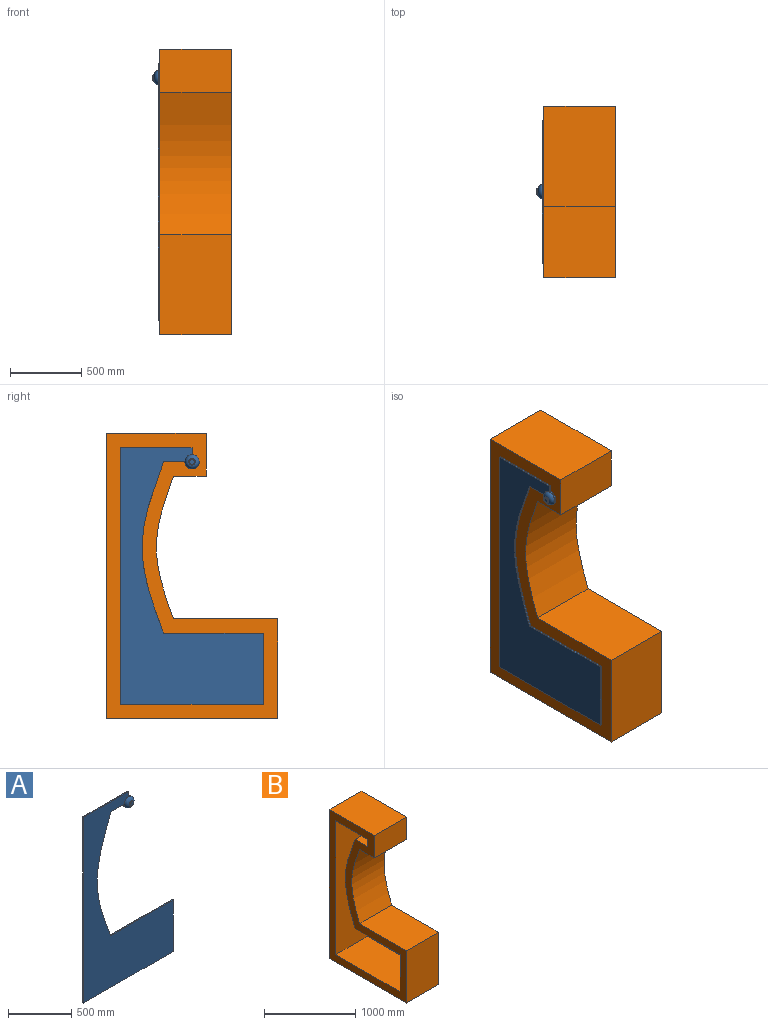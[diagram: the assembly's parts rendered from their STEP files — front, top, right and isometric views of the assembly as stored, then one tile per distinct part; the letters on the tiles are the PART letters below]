
ASSEMBLY  parts=2 mates=1
PART A: 15 faces, bbox 1000x50x1800 mm
  f0: plane 1000x10mm, normal (0,0,-1), area 10000mm2, adj f1,f7,f8,f9
  f1: plane 1800x10mm, normal (-1,0,0), area 18000mm2, adj f0,f2,f8,f9
  f2: plane 500x10mm, normal (0,0,1), area 5000mm2, adj f1,f3,f8,f9
  f3: plane 50x10mm, normal (1,0,0), area 500mm2, adj f2,f8,f9,f11
  f4: plane 150x10mm, normal (0,0,-1), area 1500mm2, adj f5,f8,f9,f11
  f5: extruded ~1200x150mm, area 12438.6mm2, adj f4,f6,f8,f9
  f6: plane 700x10mm, normal (0,0,1), area 7000mm2, adj f5,f7,f8,f9
  f7: plane 500x10mm, normal (1,0,0), area 5000mm2, adj f0,f6,f8,f9
  f8: plane 1800x1000mm, normal (0,1,0), area 803391.4mm2, adj f0,f1,f2,f3,f4,f5,f6,f7
  f9: plane 1800x1000mm, normal (0,-1,0), area 795537.4mm2, adj f0,f1,f2,f3,f4,f5,f6,f7
  f10: torus R=20mm, axis (0,-1,0), area 11576.6mm2, adj f9,f11,f12
  f11: cylinder r=50mm len=100mm, axis (0,-1,0), area 2356.2mm2, adj f3,f4,f8,f10
  f12: cone r=20mm half-angle=45deg, axis (0,-1,0), area 269.8mm2, adj f10,f14
  f13: plane 35.86x35.86mm, normal (0,-1,0), area 1009.9mm2, adj f14
  f14: torus R=17.93mm, axis (0,-1,0), area 1595.3mm2, adj f12,f13
PART B: 19 faces, bbox 500x1200x2000 mm
  f0: plane 495x200mm, normal (0,0,1), area 99000mm2, adj f1,f12,f17,f18
  f1: extruded ~1200x495mm, area 615712.1mm2, adj f0,f2,f12,f18
  f2: plane 700x495mm, normal (0,0,-1), area 346500mm2, adj f1,f12,f13,f18
  f3: plane 730.6x500mm, normal (0,0,1), area 365302.1mm2, adj f4,f8,f11,f12
  f4: plane 700x500mm, normal (0,-1,0), area 350000mm2, adj f3,f5,f11,f12
  f5: plane 1200x500mm, normal (0,0,-1), area 600000mm2, adj f4,f6,f11,f12
  f6: plane 2000x500mm, normal (0,1,0), area 1000000mm2, adj f5,f7,f11,f12
  f7: plane 700x500mm, normal (0,0,1), area 350000mm2, adj f6,f9,f11,f12
  f8: extruded ~1000x500mm, area 516859.4mm2, adj f3,f10,f11,f12
  f9: plane 500x300mm, normal (0,-1,0), area 150000mm2, adj f7,f10,f11,f12
  f10: plane 500x230.6mm, normal (0,0,-1), area 115302.1mm2, adj f8,f9,f11,f12
  f11: plane 2000x1200mm, normal (1,0,0), area 1444454mm2, adj f3,f4,f5,f6,f7,f8,f9,f10
  f12: plane 2000x1200mm, normal (-1,0,0), area 646953.1mm2, adj f0,f1,f2,f3,f4,f5,f6,f7
  f13: plane 500x495mm, normal (0,1,0), area 247500mm2, adj f2,f12,f14,f18
  f14: plane 1000x495mm, normal (0,0,1), area 495000mm2, adj f12,f13,f15,f18
  f15: plane 1800x495mm, normal (0,-1,0), area 891000mm2, adj f12,f14,f16,f18
  f16: plane 500x495mm, normal (0,0,-1), area 247500mm2, adj f12,f15,f17,f18
  f17: plane 495x100mm, normal (0,1,0), area 49500mm2, adj f0,f12,f16,f18
  f18: plane 1800x1000mm, normal (-1,0,0), area 797500.9mm2, adj f0,f1,f2,f13,f14,f15,f16,f17
PLACE A rot(axis=(0,0,-1),90deg) t=(-1138.81,-1209.02,571.63)mm
PLACE B t=(-648.81,-1085.99,49.41)mm
MATE fastened A.f8 <-> B.f12  axis (1,0,0) through (-1148.81,-785.99,-2050.59)mm
